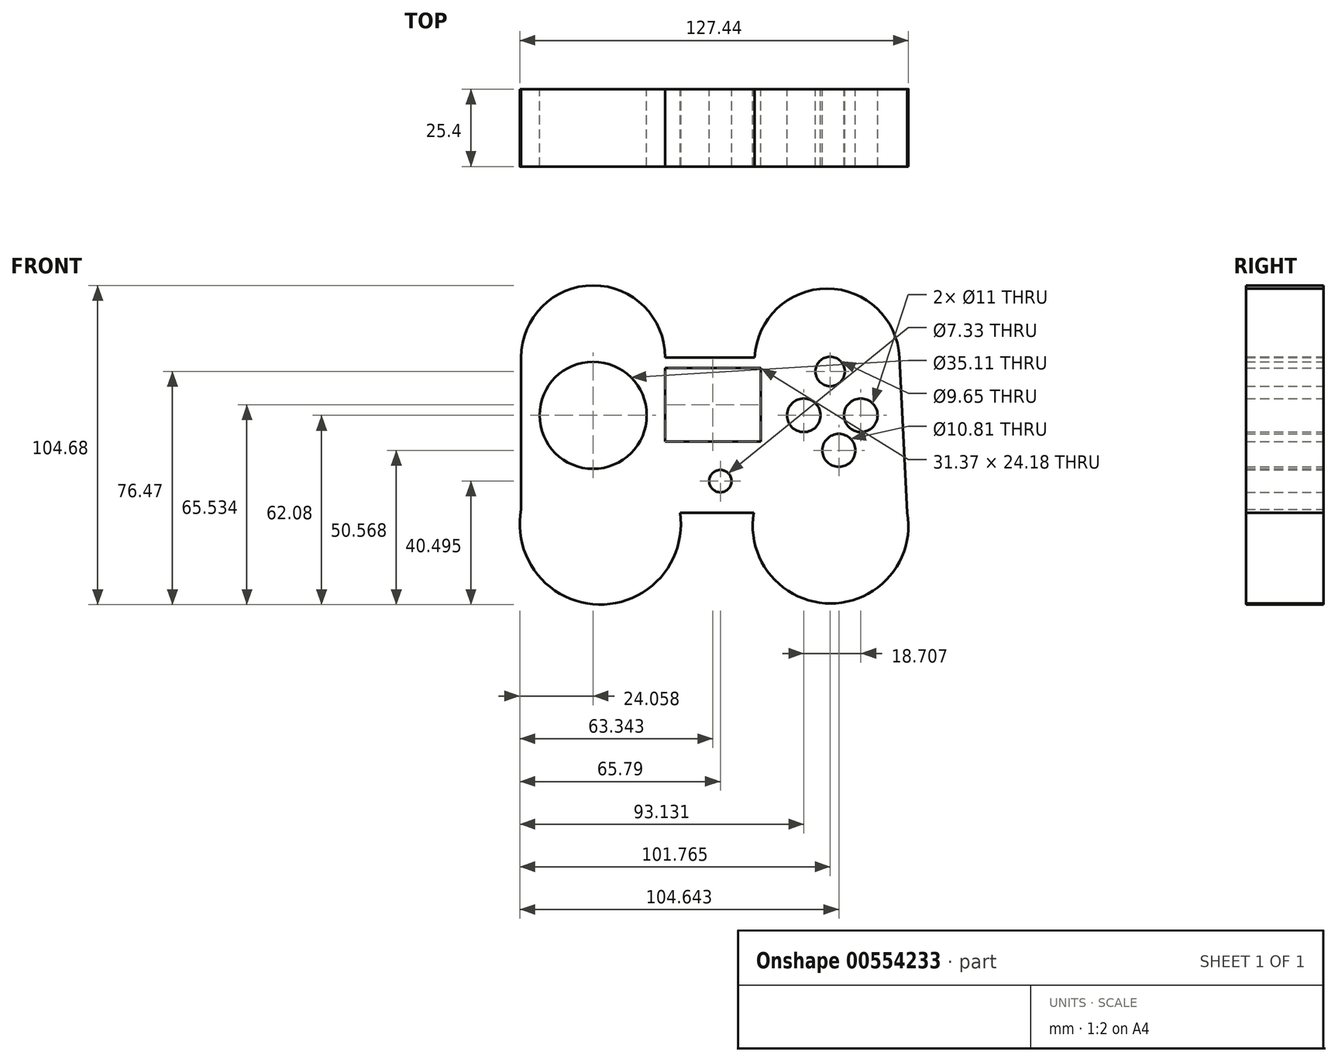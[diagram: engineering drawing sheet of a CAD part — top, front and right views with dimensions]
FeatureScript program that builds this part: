
annotation { "Feature Type Name" : "Feature", "Feature Type Description" : "" }
export const myFeature = defineFeature(function(context is Context, id is Id, definition is map)
    precondition{}
    {
        {
            var Q0;
            Q0=qCreatedBy(makeId("Front.planeOp"),FACE);
            var sketch = newSketch(context, id + "F0", { "sketchPlane" : qUnion([Q0])});
            skArc(sketch, "E0", {"start": v(-58.71, -30.8) * mm, "mid": v(-33.34, -62.08) * mm, "end": v(-6.62, -31.95) * mm});
            skArc(sketch, "E1", {"start": v(17.56, -31.95) * mm, "mid": v(42.74, -61.71) * mm, "end": v(67.92, -31.95) * mm});
            skLineSegment(sketch, "E2", {"start": v(-6.62, -31.95) * mm, "end": v(17.56, -31.95) * mm});
            skLineSegment(sketch, "E3", {"start": v(-58.71, -30.8) * mm, "end": v(-58.71, 19) * mm});
            skLineSegment(sketch, "E4", {"start": v(67.92, -31.95) * mm, "end": v(65.33, 19) * mm});
            skArc(sketch, "E5", {"start": v(-11.51, 19) * mm, "mid": v(-35.11, 42.6) * mm, "end": v(-58.71, 19) * mm});
            skArc(sketch, "E6", {"start": v(65.33, 19) * mm, "mid": v(41.59, 41.56) * mm, "end": v(17.84, 19) * mm});
            skLineSegment(sketch, "E7", {"start": v(-11.51, 19) * mm, "end": v(17.84, 19) * mm});
            skCircle(sketch, "E8", {"center": v(6.62, -21.59) * mm, "radius": 3.66 * mm});
            skLineSegment(sketch, "E9.bottom", {"start": v(-11.51, 15.54) * mm, "end": v(19.86, 15.54) * mm});
            skLineSegment(sketch, "E9.top", {"start": v(-11.51, -8.63) * mm, "end": v(19.86, -8.63) * mm});
            skLineSegment(sketch, "E9.left", {"start": v(-11.51, 15.54) * mm, "end": v(-11.51, -8.63) * mm});
            skLineSegment(sketch, "E9.right", {"start": v(19.86, 15.54) * mm, "end": v(19.86, -8.63) * mm});
            skLineSegment(sketch, "E10.bottom", {"start": v(19.86, -8.63) * mm, "end": v(-11.51, -8.63) * mm});
            skLineSegment(sketch, "E10.top", {"start": v(19.86, 15.54) * mm, "end": v(-11.51, 15.54) * mm});
            skLineSegment(sketch, "E10.left", {"start": v(19.86, -8.63) * mm, "end": v(19.86, 15.54) * mm});
            skLineSegment(sketch, "E10.right", {"start": v(-11.51, -8.63) * mm, "end": v(-11.51, 15.54) * mm});
            skCircle(sketch, "E11", {"center": v(-35.11, 0) * mm, "radius": 17.56 * mm});
            skCircle(sketch, "E12", {"center": v(42.6, 14.4) * mm, "radius": 4.82 * mm});
            skCircle(sketch, "E13", {"center": v(52.67, 0) * mm, "radius": 5.5 * mm});
            skCircle(sketch, "E14", {"center": v(33.96, 0) * mm, "radius": 5.5 * mm});
            skCircle(sketch, "E15", {"center": v(45.47, -11.51) * mm, "radius": 5.4 * mm});
            skLineSegment(sketch, "E16", {"start": v(-52.13, 4.33) * mm, "end": v(-37.13, 4.33) * mm});
            skLineSegment(sketch, "E17", {"start": v(-52.47, -2.64) * mm, "end": v(-36.55, -2.64) * mm});
            skLineSegment(sketch, "E18", {"start": v(-36.55, -2.64) * mm, "end": v(-36.55, -17.5) * mm});
            skLineSegment(sketch, "E19", {"start": v(-30.5, -2.64) * mm, "end": v(-30.5, -16.94) * mm});
            skLineSegment(sketch, "E20", {"start": v(-30.5, -2.64) * mm, "end": v(-17.76, -2.64) * mm});
            skLineSegment(sketch, "E21", {"start": v(-30.22, 4.9) * mm, "end": v(-18.25, 4.9) * mm});
            skLineSegment(sketch, "E22", {"start": v(-30.22, 4.9) * mm, "end": v(-30.22, 16.86) * mm});
            skLineSegment(sketch, "E23", {"start": v(-37.13, 4.33) * mm, "end": v(-37.13, 17.44) * mm});
            skSolve(sketch);
        }
        {
            var Q0;
            Q0=makeQuery(id+"F0.imprint","IMPRINT",FACE,{"disambiguationData":[TD([[makeQuery(id+"F0.imprint","IMPRINT",EDGE,{"derivedFrom":sQuery(id+"F0.wireOp",EDGE,"E0")}),1.0]])]});
            extrude(context, id + "F1", {"entities" : qUnion([Q0]), "depth" : 25.4 * mm, "offsetDistance" : 25.4 * mm});
        }
    });
